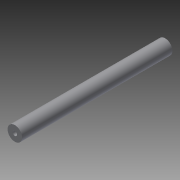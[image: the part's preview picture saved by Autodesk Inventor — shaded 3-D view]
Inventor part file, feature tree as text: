
AUTODESK INVENTOR PART (.ipt)
format: ipt  version: 2013 (Build 170138000, 138)  size: 73,216 bytes
history: native  units: in
note: dims shown in document units (in); Inventor stores cm internally (conversion verified against a paired STEP export)
features: extrude x1, sketch x1
ambient origin geometry x8: Origin, YZ Plane, XZ Plane, XY Plane, X Axis, Y Axis, Z Axis, Center Point
bodies: Solid1 (feature_tree)
feature tree (2):
  extrude  "Extrusion1"  Depth=0.75in
  sketch  "Sketch1"  dims[d0=2.5in d1=0.75in d2=25.875in d3=0.0in]
